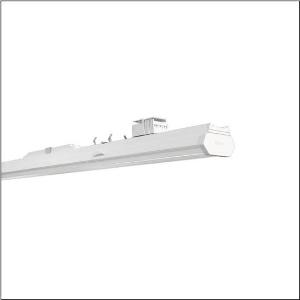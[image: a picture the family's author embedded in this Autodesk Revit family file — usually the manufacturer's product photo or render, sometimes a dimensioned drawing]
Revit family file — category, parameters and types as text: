
# Revit family: licross_r__11_protected_ho_51td12cn4exm_9b5e
name_source: partatom
category: Lighting Fixtures
units: mm (PartAtom-declared; Revit-internal decimal feet)

## family parameters
Cut with Voids When Loaded = No
Host = Face
Light Source = No
Part Type = Normal
Room Calculation Point = No
Round Connector Dimension = Use Diameter
Shared = No

## types (1)
- --- (1 x LED, 14240 lm, 77.6 W, 4000K)
    Apparent Load = 78 VA
    CIE Flux Codes = 70 91 97 98 100
    Color Rendering = 80
    Color Temperature = 4000K
    Default Elevation = 1800 mm
    Description = Licross® 11 Protected HO, luminaire insert, of sheet steel, galvanised, coil coated, white, length: 1.500mm, width: 90mm, height: 101mm, LED rated luminous flux: 14.240lm, light colour: 840, control gear: ON/OFF Multilumen, CLOi, with plug, 3-pole, with phase selection, mains connection: 220..240V, AC, 50/60Hz, start of lifetime: 78W, end of service life: 87W, halogen-free wiring, primary light control with lens, of plastic, primary optical cover: cover, of PMMA, light emission: direct distribution, primary light characteristic: symmetric, protection rating (complete): IP54, insulation class (complete): insulation class I (protective earthing), certification: CE, ENEC, VDE, UKCA, protection symbol: D if used in an environment with non-conductive dust loads with corresponding accessories, impact resistance: IK06, permissible ambient temperature for indoor applications: -35..+35°C, corresponds to IFS (International Featured Standards) requirements for safety and quality in the food industry, reducing of maximum allowable ambient temperature of 5°C with ceiling mounting, LABS conformity tested according to VDMA 24364:2018-05, packaging unit: 1 piece
    Height = 92 mm
    Lamp = 1 x LED
    Lamp Light Flux = 14240 lm
    Lamp Power = 77.6 W
    Lamp count = 1
    Length = 1500 mm
    Luminous efficacy = 184 lm/W
    Manufacturer = Siteco
    ModVariant = No
    Model = 51TD12CN4EXM
    Mounting Place = Ceiling
    Mounting Type = Pendant
    Number of Poles = 1
    OnlyDefault = Yes
    Power Factor = 1
    Product Name = Licross® 11 Protected HO
    Product group = luminaire insert
    ProductGroupID = 901
    Protection Class = Protection class I
    Protection Degree = IP 54
    RLX_Detail_Level = 1
    RLX_Emergency_Light_Flux = 0 lm
    RLX_Emergency_Type = 0
    RLX_Emergency_Type_DB = No
    RlxData = <blob elided: 22169 chars, md5=9c80f218>
    Socket = socket
    Standby Power = 0 W
    System Light Flux = 14240 lm
    System Power = 78 W
    Type Comments = factory setting: luminous flux: 100 % | (A | C | E) | 181 mA
    Type Image = l_1256145.jpg
    URL = http://relux.com
    VarID = @adj_038157
    Voltage = 0 V
    Weight = 0.00 kg
    Width = 88 mm

## geometry (parser evidence)
native form markers: Blend x4, Sweep x11
no freeform markers — native parametric forms only
